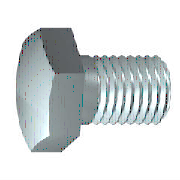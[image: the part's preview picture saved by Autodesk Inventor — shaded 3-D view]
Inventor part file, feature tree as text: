
AUTODESK INVENTOR PART (.ipt)
format: ipt  version: 2023.1 (Build 271208000, 208)  size: 210,432 bytes
history: native  units: mm (DEFAULTED — no unit token found)
features: sketch x4, other x3, revolve x2, extrude x2, fillet x1
ambient origin geometry x8: Origin, YZ Plane, XZ Plane, XY Plane, X Axis, Y Axis, Z Axis, Center Point
bodies: Solid1 (feature_tree)
feature tree (12):
  revolve  "Revolution1"  Angle=45.0deg
  extrude  "Extrusion1"  TaperAngle=60.0deg  [1 undecoded]
  revolve  "Revolution2"  Angle=30.0deg
  extrude  "Extrusion2"  TaperAngle=0.0deg  [1 undecoded]
  other  "MSC_A1"
  other  "MSC_PF1"
  other  "MSC_PT1"
  fillet  "Fillet1"  [1 undecoded]
  sketch  "Sketch2"  dims[d3=30.0deg d5=45.0deg]
  sketch  "Sketch3"  dims[d8=90.0deg d9=60.0deg]
  sketch  "Sketch4"  dims[d13=0.0mm d14=30.0deg]
  sketch  "Sketch5"  dims[d16=90.0deg d18=0.0mm d22=0.0mm d23=0.0mm d25=0.0mm d26=0.0mm d27=18.0mm d28=2.0mm d29=0.0mm d30=0.6mm d31=0.0mm]
note: 3 required parameter values undecoded (feature->parameter linkage not recoverable at this tier; creation-order binding heuristic only, values carry confidence <= 0.55)
